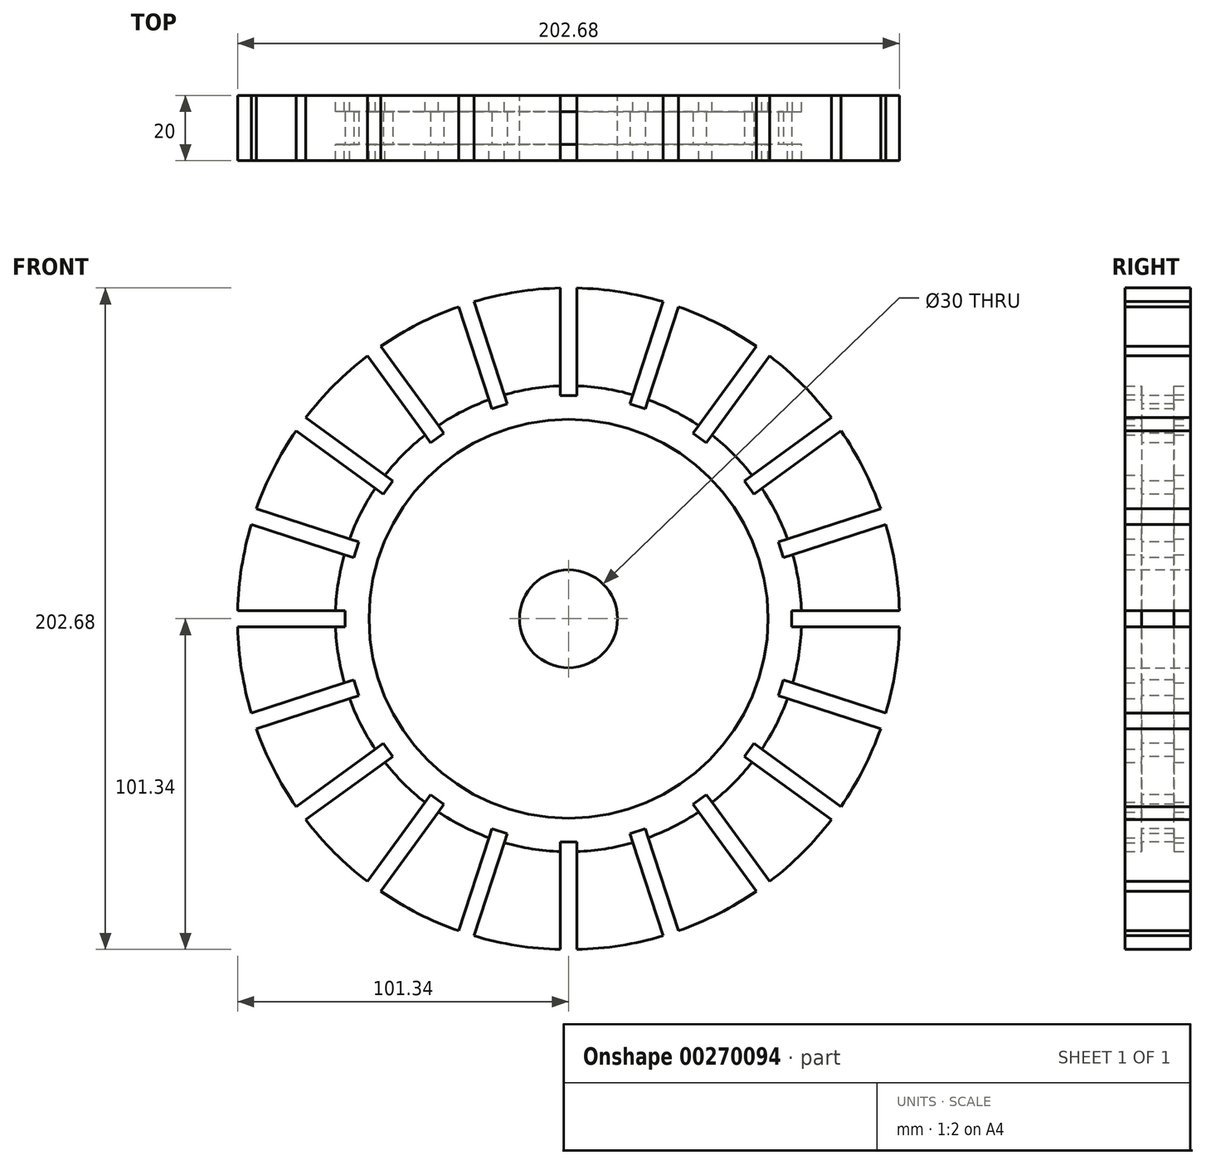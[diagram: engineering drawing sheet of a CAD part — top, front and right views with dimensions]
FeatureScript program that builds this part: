
annotation { "Feature Type Name" : "Feature", "Feature Type Description" : "" }
export const myFeature = defineFeature(function(context is Context, id is Id, definition is map)
    precondition{}
    {
        {
            var Q0;
            Q0=qCreatedBy(makeId("Right.planeOp"),FACE);
            var sketch = newSketch(context, id + "F0", { "sketchPlane" : qUnion([Q0])});
            skLineSegment(sketch, "E0", {"start": v(10, 15) * mm, "end": v(10, 61.1) * mm});
            skLineSegment(sketch, "E1", {"start": v(10, 61.1) * mm, "end": v(5, 61.1) * mm});
            skLineSegment(sketch, "E2", {"start": v(5, 61.1) * mm, "end": v(5, 71.4) * mm});
            skLineSegment(sketch, "E3", {"start": v(5, 71.4) * mm, "end": v(10, 71.4) * mm});
            skLineSegment(sketch, "E4", {"start": v(10, 71.4) * mm, "end": v(10, 101.37) * mm});
            skLineSegment(sketch, "E5", {"start": v(10, 101.37) * mm, "end": v(-10, 101.37) * mm});
            skLineSegment(sketch, "E6", {"start": v(-10, 15) * mm, "end": v(10, 15) * mm});
            skLineSegment(sketch, "E7", {"start": v(-10, 101.37) * mm, "end": v(-10, 71.4) * mm});
            skLineSegment(sketch, "E8", {"start": v(-10, 71.4) * mm, "end": v(-5, 71.4) * mm});
            skLineSegment(sketch, "E9", {"start": v(-5, 71.4) * mm, "end": v(-5, 61.1) * mm});
            skLineSegment(sketch, "E10", {"start": v(-5, 61.1) * mm, "end": v(-10, 61.1) * mm});
            skLineSegment(sketch, "E11", {"start": v(-10, 61.1) * mm, "end": v(-10, 15) * mm});
            skPoint(sketch, "E12", {"position": v(0, 15) * mm});
            skLineSegment(sketch, "E13", {"start": v(0, 0) * mm, "end": v(-55.9, 0) * mm, "construction": true});
            skSolve(sketch);
        }
        {
            var Q0;
            Q0=makeQuery(id+"F0.imprint","IMPRINT",FACE,{"disambiguationData":[TD([[makeQuery(id+"F0.imprint","IMPRINT",EDGE,{"derivedFrom":sQuery(id+"F0.wireOp",EDGE,"E0")}),1.0]])]});
            var Q1;
            Q1=sQuery(id+"F0.wireOp",EDGE,"E13");
            revolve(context, id + "F1", {"entities" : qUnion([Q0]), "axis" : qUnion([Q1]), "revolveType" : RevolveType.FULL});
        }
        {
            var Q0;
            Q0=makeQuery(id+"F1.opRevolve","SWEPT_FACE",FACE,{"disambiguationData":[OSD([sQuery(id+"F0.wireOp",EDGE,"E7")])]});
            var sketch = newSketch(context, id + "F2", { "sketchPlane" : qUnion([Q0])});
            skLineSegment(sketch, "E14", {"start": v(0, 0) * mm, "end": v(0, 127.9) * mm, "construction": true});
            skLineSegment(sketch, "E15.bottom", {"start": v(-2.5, 101.37) * mm, "end": v(2.5, 101.37) * mm});
            skLineSegment(sketch, "E15.top", {"start": v(-2.5, 68.4) * mm, "end": v(2.5, 68.4) * mm});
            skLineSegment(sketch, "E15.left", {"start": v(-2.5, 101.37) * mm, "end": v(-2.5, 68.4) * mm});
            skLineSegment(sketch, "E15.right", {"start": v(2.5, 101.37) * mm, "end": v(2.5, 68.4) * mm});
            skPoint(sketch, "E16", {"position": v(0, 101.37) * mm});
            skLineSegment(sketch, "E17", {"start": v(-18.81, 71.4) * mm, "end": v(18.81, 71.4) * mm, "construction": true});
            skPoint(sketch, "E18", {"position": v(0, 71.4) * mm});
            skLineSegment(sketch, "E19.1.0", {"start": v(-28.95, 97.18) * mm, "end": v(-18.76, 65.82) * mm});
            skLineSegment(sketch, "E19.1.1", {"start": v(-33.7, 95.64) * mm, "end": v(-23.51, 64.27) * mm});
            skLineSegment(sketch, "E19.1.2", {"start": v(-33.7, 95.64) * mm, "end": v(-28.95, 97.18) * mm});
            skLineSegment(sketch, "E19.1.3", {"start": v(-23.51, 64.27) * mm, "end": v(-18.76, 65.82) * mm});
            skLineSegment(sketch, "E19.2.0", {"start": v(-57.56, 83.48) * mm, "end": v(-38.18, 56.8) * mm});
            skLineSegment(sketch, "E19.2.1", {"start": v(-61.6, 80.54) * mm, "end": v(-42.22, 53.86) * mm});
            skLineSegment(sketch, "E19.2.2", {"start": v(-61.6, 80.54) * mm, "end": v(-57.56, 83.48) * mm});
            skLineSegment(sketch, "E19.2.3", {"start": v(-42.22, 53.86) * mm, "end": v(-38.18, 56.8) * mm});
            skLineSegment(sketch, "E19.3.0", {"start": v(-80.54, 61.6) * mm, "end": v(-53.86, 42.22) * mm});
            skLineSegment(sketch, "E19.3.1", {"start": v(-83.48, 57.56) * mm, "end": v(-56.8, 38.18) * mm});
            skLineSegment(sketch, "E19.3.2", {"start": v(-83.48, 57.56) * mm, "end": v(-80.54, 61.6) * mm});
            skLineSegment(sketch, "E19.3.3", {"start": v(-56.8, 38.18) * mm, "end": v(-53.86, 42.22) * mm});
            skLineSegment(sketch, "E19.4.0", {"start": v(-95.64, 33.7) * mm, "end": v(-64.27, 23.51) * mm});
            skLineSegment(sketch, "E19.4.1", {"start": v(-97.18, 28.95) * mm, "end": v(-65.82, 18.76) * mm});
            skLineSegment(sketch, "E19.4.2", {"start": v(-97.18, 28.95) * mm, "end": v(-95.64, 33.7) * mm});
            skLineSegment(sketch, "E19.4.3", {"start": v(-65.82, 18.76) * mm, "end": v(-64.27, 23.51) * mm});
            skLineSegment(sketch, "E19.5.0", {"start": v(-101.37, 2.5) * mm, "end": v(-68.4, 2.5) * mm});
            skLineSegment(sketch, "E19.5.1", {"start": v(-101.37, -2.5) * mm, "end": v(-68.4, -2.5) * mm});
            skLineSegment(sketch, "E19.5.2", {"start": v(-101.37, -2.5) * mm, "end": v(-101.37, 2.5) * mm});
            skLineSegment(sketch, "E19.5.3", {"start": v(-68.4, -2.5) * mm, "end": v(-68.4, 2.5) * mm});
            skLineSegment(sketch, "E19.6.0", {"start": v(-97.18, -28.95) * mm, "end": v(-65.82, -18.76) * mm});
            skLineSegment(sketch, "E19.6.1", {"start": v(-95.64, -33.7) * mm, "end": v(-64.27, -23.51) * mm});
            skLineSegment(sketch, "E19.6.2", {"start": v(-95.64, -33.7) * mm, "end": v(-97.18, -28.95) * mm});
            skLineSegment(sketch, "E19.6.3", {"start": v(-64.27, -23.51) * mm, "end": v(-65.82, -18.76) * mm});
            skLineSegment(sketch, "E19.7.0", {"start": v(-83.48, -57.56) * mm, "end": v(-56.8, -38.18) * mm});
            skLineSegment(sketch, "E19.7.1", {"start": v(-80.54, -61.6) * mm, "end": v(-53.86, -42.22) * mm});
            skLineSegment(sketch, "E19.7.2", {"start": v(-80.54, -61.6) * mm, "end": v(-83.48, -57.56) * mm});
            skLineSegment(sketch, "E19.7.3", {"start": v(-53.86, -42.22) * mm, "end": v(-56.8, -38.18) * mm});
            skLineSegment(sketch, "E19.8.0", {"start": v(-61.6, -80.54) * mm, "end": v(-42.22, -53.86) * mm});
            skLineSegment(sketch, "E19.8.1", {"start": v(-57.56, -83.48) * mm, "end": v(-38.18, -56.8) * mm});
            skLineSegment(sketch, "E19.8.2", {"start": v(-57.56, -83.48) * mm, "end": v(-61.6, -80.54) * mm});
            skLineSegment(sketch, "E19.8.3", {"start": v(-38.18, -56.8) * mm, "end": v(-42.22, -53.86) * mm});
            skLineSegment(sketch, "E19.9.0", {"start": v(-33.7, -95.64) * mm, "end": v(-23.51, -64.27) * mm});
            skLineSegment(sketch, "E19.9.1", {"start": v(-28.95, -97.18) * mm, "end": v(-18.76, -65.82) * mm});
            skLineSegment(sketch, "E19.9.2", {"start": v(-28.95, -97.18) * mm, "end": v(-33.7, -95.64) * mm});
            skLineSegment(sketch, "E19.9.3", {"start": v(-18.76, -65.82) * mm, "end": v(-23.51, -64.27) * mm});
            skLineSegment(sketch, "E19.10.0", {"start": v(-2.5, -101.37) * mm, "end": v(-2.5, -68.4) * mm});
            skLineSegment(sketch, "E19.10.1", {"start": v(2.5, -101.37) * mm, "end": v(2.5, -68.4) * mm});
            skLineSegment(sketch, "E19.10.2", {"start": v(2.5, -101.37) * mm, "end": v(-2.5, -101.37) * mm});
            skLineSegment(sketch, "E19.10.3", {"start": v(2.5, -68.4) * mm, "end": v(-2.5, -68.4) * mm});
            skLineSegment(sketch, "E19.11.0", {"start": v(28.95, -97.18) * mm, "end": v(18.76, -65.82) * mm});
            skLineSegment(sketch, "E19.11.1", {"start": v(33.7, -95.64) * mm, "end": v(23.51, -64.27) * mm});
            skLineSegment(sketch, "E19.11.2", {"start": v(33.7, -95.64) * mm, "end": v(28.95, -97.18) * mm});
            skLineSegment(sketch, "E19.11.3", {"start": v(23.51, -64.27) * mm, "end": v(18.76, -65.82) * mm});
            skLineSegment(sketch, "E19.12.0", {"start": v(57.56, -83.48) * mm, "end": v(38.18, -56.8) * mm});
            skLineSegment(sketch, "E19.12.1", {"start": v(61.6, -80.54) * mm, "end": v(42.22, -53.86) * mm});
            skLineSegment(sketch, "E19.12.2", {"start": v(61.6, -80.54) * mm, "end": v(57.56, -83.48) * mm});
            skLineSegment(sketch, "E19.12.3", {"start": v(42.22, -53.86) * mm, "end": v(38.18, -56.8) * mm});
            skLineSegment(sketch, "E19.13.0", {"start": v(80.54, -61.6) * mm, "end": v(53.86, -42.22) * mm});
            skLineSegment(sketch, "E19.13.1", {"start": v(83.48, -57.56) * mm, "end": v(56.8, -38.18) * mm});
            skLineSegment(sketch, "E19.13.2", {"start": v(83.48, -57.56) * mm, "end": v(80.54, -61.6) * mm});
            skLineSegment(sketch, "E19.13.3", {"start": v(56.8, -38.18) * mm, "end": v(53.86, -42.22) * mm});
            skLineSegment(sketch, "E19.14.0", {"start": v(95.64, -33.7) * mm, "end": v(64.27, -23.51) * mm});
            skLineSegment(sketch, "E19.14.1", {"start": v(97.18, -28.95) * mm, "end": v(65.82, -18.76) * mm});
            skLineSegment(sketch, "E19.14.2", {"start": v(97.18, -28.95) * mm, "end": v(95.64, -33.7) * mm});
            skLineSegment(sketch, "E19.14.3", {"start": v(65.82, -18.76) * mm, "end": v(64.27, -23.51) * mm});
            skLineSegment(sketch, "E19.15.0", {"start": v(101.37, -2.5) * mm, "end": v(68.4, -2.5) * mm});
            skLineSegment(sketch, "E19.15.1", {"start": v(101.37, 2.5) * mm, "end": v(68.4, 2.5) * mm});
            skLineSegment(sketch, "E19.15.2", {"start": v(101.37, 2.5) * mm, "end": v(101.37, -2.5) * mm});
            skLineSegment(sketch, "E19.15.3", {"start": v(68.4, 2.5) * mm, "end": v(68.4, -2.5) * mm});
            skLineSegment(sketch, "E19.16.0", {"start": v(97.18, 28.95) * mm, "end": v(65.82, 18.76) * mm});
            skLineSegment(sketch, "E19.16.1", {"start": v(95.64, 33.7) * mm, "end": v(64.27, 23.51) * mm});
            skLineSegment(sketch, "E19.16.2", {"start": v(95.64, 33.7) * mm, "end": v(97.18, 28.95) * mm});
            skLineSegment(sketch, "E19.16.3", {"start": v(64.27, 23.51) * mm, "end": v(65.82, 18.76) * mm});
            skLineSegment(sketch, "E19.17.0", {"start": v(83.48, 57.56) * mm, "end": v(56.8, 38.18) * mm});
            skLineSegment(sketch, "E19.17.1", {"start": v(80.54, 61.6) * mm, "end": v(53.86, 42.22) * mm});
            skLineSegment(sketch, "E19.17.2", {"start": v(80.54, 61.6) * mm, "end": v(83.48, 57.56) * mm});
            skLineSegment(sketch, "E19.17.3", {"start": v(53.86, 42.22) * mm, "end": v(56.8, 38.18) * mm});
            skLineSegment(sketch, "E19.18.0", {"start": v(61.6, 80.54) * mm, "end": v(42.22, 53.86) * mm});
            skLineSegment(sketch, "E19.18.1", {"start": v(57.56, 83.48) * mm, "end": v(38.18, 56.8) * mm});
            skLineSegment(sketch, "E19.18.2", {"start": v(57.56, 83.48) * mm, "end": v(61.6, 80.54) * mm});
            skLineSegment(sketch, "E19.18.3", {"start": v(38.18, 56.8) * mm, "end": v(42.22, 53.86) * mm});
            skLineSegment(sketch, "E19.19.0", {"start": v(33.7, 95.64) * mm, "end": v(23.51, 64.27) * mm});
            skLineSegment(sketch, "E19.19.1", {"start": v(28.95, 97.18) * mm, "end": v(18.76, 65.82) * mm});
            skLineSegment(sketch, "E19.19.2", {"start": v(28.95, 97.18) * mm, "end": v(33.7, 95.64) * mm});
            skLineSegment(sketch, "E19.19.3", {"start": v(18.76, 65.82) * mm, "end": v(23.51, 64.27) * mm});
            skPoint(sketch, "E19.center", {"position": v(0, 0) * mm});
            skSolve(sketch);
        }
        {
            var Q0;
            {var subQ0=sQuery(id+"F0.wireOp",EDGE,"E7");var subQ1=makeQuery(id+"F1.opRevolve","SWEPT_EDGE",EDGE,{"disambiguationData":[OSD([sQuery(id+"F0.wireOp",EDGE,"E5"),subQ0])]});var subQ5=sQuery(id+"F2.wireOp",EDGE,"E15.left");var subQ6=makeQuery(id+"F2.imprint","INTERSECT",VERTEX,{"derivedFrom":[subQ1,subQ5]});Q0=makeQuery(id+"F2.imprint","IMPRINT",FACE,{"disambiguationData":[TD([[makeQuery(id+"F2.imprint","IMPRINT",EDGE,{"disambiguationData":[TD([[subQ6,-1.0]])],"derivedFrom":subQ5}),1.0]])]});}
            var Q1;
            {var subQ0=sQuery(id+"F2.wireOp",EDGE,"E15.top");Q1=makeQuery(id+"F2.imprint","IMPRINT",FACE,{"disambiguationData":[TD([[makeQuery(id+"F2.imprint","IMPRINT",EDGE,{"derivedFrom":subQ0}),1.0]])]});}
            var Q2;
            {var subQ1=sQuery(id+"F0.wireOp",EDGE,"E7");var subQ2=makeQuery(id+"F1.opRevolve","SWEPT_EDGE",EDGE,{"disambiguationData":[OSD([sQuery(id+"F0.wireOp",EDGE,"E5"),subQ1])]});var subQ5=sQuery(id+"F2.wireOp",EDGE,"E19.19.0");var subQ6=makeQuery(id+"F2.imprint","INTERSECT",VERTEX,{"derivedFrom":[subQ2,subQ5]});Q2=makeQuery(id+"F2.imprint","IMPRINT",FACE,{"disambiguationData":[TD([[makeQuery(id+"F2.imprint","IMPRINT",EDGE,{"disambiguationData":[TD([[subQ6,-1.0]])],"derivedFrom":subQ5}),-1.0]])]});}
            var Q3;
            {var subQ0=sQuery(id+"F2.wireOp",EDGE,"E19.19.3");Q3=makeQuery(id+"F2.imprint","IMPRINT",FACE,{"disambiguationData":[TD([[makeQuery(id+"F2.imprint","IMPRINT",EDGE,{"derivedFrom":subQ0}),1.0]])]});}
            var Q4;
            {var subQ1=sQuery(id+"F0.wireOp",EDGE,"E7");var subQ2=makeQuery(id+"F1.opRevolve","SWEPT_EDGE",EDGE,{"disambiguationData":[OSD([sQuery(id+"F0.wireOp",EDGE,"E5"),subQ1])]});var subQ5=sQuery(id+"F2.wireOp",EDGE,"E19.18.0");var subQ6=makeQuery(id+"F2.imprint","INTERSECT",VERTEX,{"derivedFrom":[subQ2,subQ5]});Q4=makeQuery(id+"F2.imprint","IMPRINT",FACE,{"disambiguationData":[TD([[makeQuery(id+"F2.imprint","IMPRINT",EDGE,{"disambiguationData":[TD([[subQ6,-1.0]])],"derivedFrom":subQ5}),-1.0]])]});}
            var Q5;
            {var subQ0=sQuery(id+"F2.wireOp",EDGE,"E19.18.3");Q5=makeQuery(id+"F2.imprint","IMPRINT",FACE,{"disambiguationData":[TD([[makeQuery(id+"F2.imprint","IMPRINT",EDGE,{"derivedFrom":subQ0}),1.0]])]});}
            var Q6;
            {var subQ1=sQuery(id+"F0.wireOp",EDGE,"E7");var subQ2=makeQuery(id+"F1.opRevolve","SWEPT_EDGE",EDGE,{"disambiguationData":[OSD([sQuery(id+"F0.wireOp",EDGE,"E5"),subQ1])]});var subQ5=sQuery(id+"F2.wireOp",EDGE,"E19.17.0");var subQ6=makeQuery(id+"F2.imprint","INTERSECT",VERTEX,{"derivedFrom":[subQ2,subQ5]});Q6=makeQuery(id+"F2.imprint","IMPRINT",FACE,{"disambiguationData":[TD([[makeQuery(id+"F2.imprint","IMPRINT",EDGE,{"disambiguationData":[TD([[subQ6,-1.0]])],"derivedFrom":subQ5}),-1.0]])]});}
            var Q7;
            {var subQ0=sQuery(id+"F2.wireOp",EDGE,"E19.17.3");Q7=makeQuery(id+"F2.imprint","IMPRINT",FACE,{"disambiguationData":[TD([[makeQuery(id+"F2.imprint","IMPRINT",EDGE,{"derivedFrom":subQ0}),1.0]])]});}
            var Q8;
            {var subQ1=sQuery(id+"F0.wireOp",EDGE,"E7");var subQ2=makeQuery(id+"F1.opRevolve","SWEPT_EDGE",EDGE,{"disambiguationData":[OSD([sQuery(id+"F0.wireOp",EDGE,"E5"),subQ1])]});var subQ7=sQuery(id+"F2.wireOp",EDGE,"E19.16.0");var subQ8=makeQuery(id+"F2.imprint","INTERSECT",VERTEX,{"derivedFrom":[subQ2,subQ7]});Q8=makeQuery(id+"F2.imprint","IMPRINT",FACE,{"disambiguationData":[TD([[makeQuery(id+"F2.imprint","IMPRINT",EDGE,{"disambiguationData":[TD([[subQ8,-1.0]])],"derivedFrom":subQ7}),-1.0]])]});}
            var Q9;
            {var subQ0=sQuery(id+"F2.wireOp",EDGE,"E19.16.3");Q9=makeQuery(id+"F2.imprint","IMPRINT",FACE,{"disambiguationData":[TD([[makeQuery(id+"F2.imprint","IMPRINT",EDGE,{"derivedFrom":subQ0}),1.0]])]});}
            var Q10;
            {var subQ1=sQuery(id+"F0.wireOp",EDGE,"E7");var subQ2=makeQuery(id+"F1.opRevolve","SWEPT_EDGE",EDGE,{"disambiguationData":[OSD([sQuery(id+"F0.wireOp",EDGE,"E5"),subQ1])]});var subQ5=sQuery(id+"F2.wireOp",EDGE,"E19.15.0");var subQ6=makeQuery(id+"F2.imprint","INTERSECT",VERTEX,{"derivedFrom":[subQ2,subQ5]});Q10=makeQuery(id+"F2.imprint","IMPRINT",FACE,{"disambiguationData":[TD([[makeQuery(id+"F2.imprint","IMPRINT",EDGE,{"disambiguationData":[TD([[subQ6,-1.0]])],"derivedFrom":subQ5}),-1.0]])]});}
            var Q11;
            {var subQ0=sQuery(id+"F2.wireOp",EDGE,"E19.15.3");Q11=makeQuery(id+"F2.imprint","IMPRINT",FACE,{"disambiguationData":[TD([[makeQuery(id+"F2.imprint","IMPRINT",EDGE,{"derivedFrom":subQ0}),1.0]])]});}
            var Q12;
            {var subQ1=sQuery(id+"F0.wireOp",EDGE,"E7");var subQ2=makeQuery(id+"F1.opRevolve","SWEPT_EDGE",EDGE,{"disambiguationData":[OSD([sQuery(id+"F0.wireOp",EDGE,"E5"),subQ1])]});var subQ5=sQuery(id+"F2.wireOp",EDGE,"E19.14.0");var subQ6=makeQuery(id+"F2.imprint","INTERSECT",VERTEX,{"derivedFrom":[subQ2,subQ5]});Q12=makeQuery(id+"F2.imprint","IMPRINT",FACE,{"disambiguationData":[TD([[makeQuery(id+"F2.imprint","IMPRINT",EDGE,{"disambiguationData":[TD([[subQ6,-1.0]])],"derivedFrom":subQ5}),-1.0]])]});}
            var Q13;
            {var subQ0=sQuery(id+"F2.wireOp",EDGE,"E19.14.3");Q13=makeQuery(id+"F2.imprint","IMPRINT",FACE,{"disambiguationData":[TD([[makeQuery(id+"F2.imprint","IMPRINT",EDGE,{"derivedFrom":subQ0}),1.0]])]});}
            var Q14;
            {var subQ1=sQuery(id+"F0.wireOp",EDGE,"E7");var subQ2=makeQuery(id+"F1.opRevolve","SWEPT_EDGE",EDGE,{"disambiguationData":[OSD([sQuery(id+"F0.wireOp",EDGE,"E5"),subQ1])]});var subQ5=sQuery(id+"F2.wireOp",EDGE,"E19.13.0");var subQ6=makeQuery(id+"F2.imprint","INTERSECT",VERTEX,{"derivedFrom":[subQ2,subQ5]});Q14=makeQuery(id+"F2.imprint","IMPRINT",FACE,{"disambiguationData":[TD([[makeQuery(id+"F2.imprint","IMPRINT",EDGE,{"disambiguationData":[TD([[subQ6,-1.0]])],"derivedFrom":subQ5}),-1.0]])]});}
            var Q15;
            {var subQ0=sQuery(id+"F2.wireOp",EDGE,"E19.13.3");Q15=makeQuery(id+"F2.imprint","IMPRINT",FACE,{"disambiguationData":[TD([[makeQuery(id+"F2.imprint","IMPRINT",EDGE,{"derivedFrom":subQ0}),1.0]])]});}
            var Q16;
            {var subQ1=sQuery(id+"F0.wireOp",EDGE,"E7");var subQ2=makeQuery(id+"F1.opRevolve","SWEPT_EDGE",EDGE,{"disambiguationData":[OSD([sQuery(id+"F0.wireOp",EDGE,"E5"),subQ1])]});var subQ7=sQuery(id+"F2.wireOp",EDGE,"E19.12.0");var subQ8=makeQuery(id+"F2.imprint","INTERSECT",VERTEX,{"derivedFrom":[subQ2,subQ7]});Q16=makeQuery(id+"F2.imprint","IMPRINT",FACE,{"disambiguationData":[TD([[makeQuery(id+"F2.imprint","IMPRINT",EDGE,{"disambiguationData":[TD([[subQ8,-1.0]])],"derivedFrom":subQ7}),-1.0]])]});}
            var Q17;
            {var subQ0=sQuery(id+"F2.wireOp",EDGE,"E19.12.3");Q17=makeQuery(id+"F2.imprint","IMPRINT",FACE,{"disambiguationData":[TD([[makeQuery(id+"F2.imprint","IMPRINT",EDGE,{"derivedFrom":subQ0}),1.0]])]});}
            var Q18;
            {var subQ1=sQuery(id+"F0.wireOp",EDGE,"E7");var subQ2=makeQuery(id+"F1.opRevolve","SWEPT_EDGE",EDGE,{"disambiguationData":[OSD([sQuery(id+"F0.wireOp",EDGE,"E5"),subQ1])]});var subQ7=sQuery(id+"F2.wireOp",EDGE,"E19.11.0");var subQ8=makeQuery(id+"F2.imprint","INTERSECT",VERTEX,{"derivedFrom":[subQ2,subQ7]});Q18=makeQuery(id+"F2.imprint","IMPRINT",FACE,{"disambiguationData":[TD([[makeQuery(id+"F2.imprint","IMPRINT",EDGE,{"disambiguationData":[TD([[subQ8,-1.0]])],"derivedFrom":subQ7}),-1.0]])]});}
            var Q19;
            {var subQ0=sQuery(id+"F2.wireOp",EDGE,"E19.11.3");Q19=makeQuery(id+"F2.imprint","IMPRINT",FACE,{"disambiguationData":[TD([[makeQuery(id+"F2.imprint","IMPRINT",EDGE,{"derivedFrom":subQ0}),1.0]])]});}
            var Q20;
            {var subQ1=sQuery(id+"F0.wireOp",EDGE,"E7");var subQ2=makeQuery(id+"F1.opRevolve","SWEPT_EDGE",EDGE,{"disambiguationData":[OSD([sQuery(id+"F0.wireOp",EDGE,"E5"),subQ1])]});var subQ7=sQuery(id+"F2.wireOp",EDGE,"E19.10.0");var subQ8=makeQuery(id+"F2.imprint","INTERSECT",VERTEX,{"derivedFrom":[subQ2,subQ7]});Q20=makeQuery(id+"F2.imprint","IMPRINT",FACE,{"disambiguationData":[TD([[makeQuery(id+"F2.imprint","IMPRINT",EDGE,{"disambiguationData":[TD([[subQ8,-1.0]])],"derivedFrom":subQ7}),-1.0]])]});}
            var Q21;
            {var subQ0=sQuery(id+"F2.wireOp",EDGE,"E19.10.3");Q21=makeQuery(id+"F2.imprint","IMPRINT",FACE,{"disambiguationData":[TD([[makeQuery(id+"F2.imprint","IMPRINT",EDGE,{"derivedFrom":subQ0}),1.0]])]});}
            var Q22;
            {var subQ1=sQuery(id+"F0.wireOp",EDGE,"E7");var subQ2=makeQuery(id+"F1.opRevolve","SWEPT_EDGE",EDGE,{"disambiguationData":[OSD([sQuery(id+"F0.wireOp",EDGE,"E5"),subQ1])]});var subQ7=sQuery(id+"F2.wireOp",EDGE,"E19.9.0");var subQ8=makeQuery(id+"F2.imprint","INTERSECT",VERTEX,{"derivedFrom":[subQ2,subQ7]});Q22=makeQuery(id+"F2.imprint","IMPRINT",FACE,{"disambiguationData":[TD([[makeQuery(id+"F2.imprint","IMPRINT",EDGE,{"disambiguationData":[TD([[subQ8,-1.0]])],"derivedFrom":subQ7}),-1.0]])]});}
            var Q23;
            {var subQ0=sQuery(id+"F2.wireOp",EDGE,"E19.9.3");Q23=makeQuery(id+"F2.imprint","IMPRINT",FACE,{"disambiguationData":[TD([[makeQuery(id+"F2.imprint","IMPRINT",EDGE,{"derivedFrom":subQ0}),1.0]])]});}
            var Q24;
            {var subQ1=sQuery(id+"F0.wireOp",EDGE,"E7");var subQ2=makeQuery(id+"F1.opRevolve","SWEPT_EDGE",EDGE,{"disambiguationData":[OSD([sQuery(id+"F0.wireOp",EDGE,"E5"),subQ1])]});var subQ5=sQuery(id+"F2.wireOp",EDGE,"E19.8.0");var subQ6=makeQuery(id+"F2.imprint","INTERSECT",VERTEX,{"derivedFrom":[subQ2,subQ5]});Q24=makeQuery(id+"F2.imprint","IMPRINT",FACE,{"disambiguationData":[TD([[makeQuery(id+"F2.imprint","IMPRINT",EDGE,{"disambiguationData":[TD([[subQ6,-1.0]])],"derivedFrom":subQ5}),-1.0]])]});}
            var Q25;
            {var subQ0=sQuery(id+"F2.wireOp",EDGE,"E19.8.3");Q25=makeQuery(id+"F2.imprint","IMPRINT",FACE,{"disambiguationData":[TD([[makeQuery(id+"F2.imprint","IMPRINT",EDGE,{"derivedFrom":subQ0}),1.0]])]});}
            var Q26;
            {var subQ0=sQuery(id+"F2.wireOp",EDGE,"E19.7.0");var subQ1=sQuery(id+"F0.wireOp",EDGE,"E7");var subQ2=makeQuery(id+"F1.opRevolve","SWEPT_EDGE",EDGE,{"disambiguationData":[OSD([sQuery(id+"F0.wireOp",EDGE,"E5"),subQ1])]});var subQ3=makeQuery(id+"F2.imprint","INTERSECT",VERTEX,{"derivedFrom":[subQ2,subQ0]});Q26=makeQuery(id+"F2.imprint","IMPRINT",FACE,{"disambiguationData":[TD([[makeQuery(id+"F2.imprint","IMPRINT",EDGE,{"disambiguationData":[TD([[subQ3,-1.0]])],"derivedFrom":subQ0}),-1.0]])]});}
            var Q27;
            {var subQ0=sQuery(id+"F2.wireOp",EDGE,"E19.7.3");Q27=makeQuery(id+"F2.imprint","IMPRINT",FACE,{"disambiguationData":[TD([[makeQuery(id+"F2.imprint","IMPRINT",EDGE,{"derivedFrom":subQ0}),1.0]])]});}
            var Q28;
            {var subQ1=sQuery(id+"F0.wireOp",EDGE,"E7");var subQ2=makeQuery(id+"F1.opRevolve","SWEPT_EDGE",EDGE,{"disambiguationData":[OSD([sQuery(id+"F0.wireOp",EDGE,"E5"),subQ1])]});var subQ5=sQuery(id+"F2.wireOp",EDGE,"E19.6.0");var subQ6=makeQuery(id+"F2.imprint","INTERSECT",VERTEX,{"derivedFrom":[subQ2,subQ5]});Q28=makeQuery(id+"F2.imprint","IMPRINT",FACE,{"disambiguationData":[TD([[makeQuery(id+"F2.imprint","IMPRINT",EDGE,{"disambiguationData":[TD([[subQ6,-1.0]])],"derivedFrom":subQ5}),-1.0]])]});}
            var Q29;
            {var subQ0=sQuery(id+"F2.wireOp",EDGE,"E19.6.3");Q29=makeQuery(id+"F2.imprint","IMPRINT",FACE,{"disambiguationData":[TD([[makeQuery(id+"F2.imprint","IMPRINT",EDGE,{"derivedFrom":subQ0}),1.0]])]});}
            var Q30;
            {var subQ1=sQuery(id+"F0.wireOp",EDGE,"E7");var subQ2=makeQuery(id+"F1.opRevolve","SWEPT_EDGE",EDGE,{"disambiguationData":[OSD([sQuery(id+"F0.wireOp",EDGE,"E5"),subQ1])]});var subQ5=sQuery(id+"F2.wireOp",EDGE,"E19.5.0");var subQ6=makeQuery(id+"F2.imprint","INTERSECT",VERTEX,{"derivedFrom":[subQ2,subQ5]});Q30=makeQuery(id+"F2.imprint","IMPRINT",FACE,{"disambiguationData":[TD([[makeQuery(id+"F2.imprint","IMPRINT",EDGE,{"disambiguationData":[TD([[subQ6,-1.0]])],"derivedFrom":subQ5}),-1.0]])]});}
            var Q31;
            {var subQ0=sQuery(id+"F2.wireOp",EDGE,"E19.5.3");Q31=makeQuery(id+"F2.imprint","IMPRINT",FACE,{"disambiguationData":[TD([[makeQuery(id+"F2.imprint","IMPRINT",EDGE,{"derivedFrom":subQ0}),1.0]])]});}
            var Q32;
            {var subQ0=sQuery(id+"F2.wireOp",EDGE,"E19.4.0");var subQ1=sQuery(id+"F0.wireOp",EDGE,"E7");var subQ2=makeQuery(id+"F1.opRevolve","SWEPT_EDGE",EDGE,{"disambiguationData":[OSD([sQuery(id+"F0.wireOp",EDGE,"E5"),subQ1])]});var subQ3=makeQuery(id+"F2.imprint","INTERSECT",VERTEX,{"derivedFrom":[subQ2,subQ0]});Q32=makeQuery(id+"F2.imprint","IMPRINT",FACE,{"disambiguationData":[TD([[makeQuery(id+"F2.imprint","IMPRINT",EDGE,{"disambiguationData":[TD([[subQ3,-1.0]])],"derivedFrom":subQ0}),-1.0]])]});}
            var Q33;
            {var subQ0=sQuery(id+"F2.wireOp",EDGE,"E19.4.3");Q33=makeQuery(id+"F2.imprint","IMPRINT",FACE,{"disambiguationData":[TD([[makeQuery(id+"F2.imprint","IMPRINT",EDGE,{"derivedFrom":subQ0}),1.0]])]});}
            var Q34;
            {var subQ1=sQuery(id+"F0.wireOp",EDGE,"E7");var subQ2=makeQuery(id+"F1.opRevolve","SWEPT_EDGE",EDGE,{"disambiguationData":[OSD([sQuery(id+"F0.wireOp",EDGE,"E5"),subQ1])]});var subQ5=sQuery(id+"F2.wireOp",EDGE,"E19.3.0");var subQ6=makeQuery(id+"F2.imprint","INTERSECT",VERTEX,{"derivedFrom":[subQ2,subQ5]});Q34=makeQuery(id+"F2.imprint","IMPRINT",FACE,{"disambiguationData":[TD([[makeQuery(id+"F2.imprint","IMPRINT",EDGE,{"disambiguationData":[TD([[subQ6,-1.0]])],"derivedFrom":subQ5}),-1.0]])]});}
            var Q35;
            {var subQ0=sQuery(id+"F2.wireOp",EDGE,"E19.3.3");Q35=makeQuery(id+"F2.imprint","IMPRINT",FACE,{"disambiguationData":[TD([[makeQuery(id+"F2.imprint","IMPRINT",EDGE,{"derivedFrom":subQ0}),1.0]])]});}
            var Q36;
            {var subQ1=sQuery(id+"F0.wireOp",EDGE,"E7");var subQ2=makeQuery(id+"F1.opRevolve","SWEPT_EDGE",EDGE,{"disambiguationData":[OSD([sQuery(id+"F0.wireOp",EDGE,"E5"),subQ1])]});var subQ7=sQuery(id+"F2.wireOp",EDGE,"E19.2.0");var subQ8=makeQuery(id+"F2.imprint","INTERSECT",VERTEX,{"derivedFrom":[subQ2,subQ7]});Q36=makeQuery(id+"F2.imprint","IMPRINT",FACE,{"disambiguationData":[TD([[makeQuery(id+"F2.imprint","IMPRINT",EDGE,{"disambiguationData":[TD([[subQ8,-1.0]])],"derivedFrom":subQ7}),-1.0]])]});}
            var Q37;
            {var subQ0=sQuery(id+"F2.wireOp",EDGE,"E19.2.3");Q37=makeQuery(id+"F2.imprint","IMPRINT",FACE,{"disambiguationData":[TD([[makeQuery(id+"F2.imprint","IMPRINT",EDGE,{"derivedFrom":subQ0}),1.0]])]});}
            var Q38;
            {var subQ1=sQuery(id+"F0.wireOp",EDGE,"E7");var subQ2=makeQuery(id+"F1.opRevolve","SWEPT_EDGE",EDGE,{"disambiguationData":[OSD([sQuery(id+"F0.wireOp",EDGE,"E5"),subQ1])]});var subQ5=sQuery(id+"F2.wireOp",EDGE,"E19.1.0");var subQ6=makeQuery(id+"F2.imprint","INTERSECT",VERTEX,{"derivedFrom":[subQ2,subQ5]});Q38=makeQuery(id+"F2.imprint","IMPRINT",FACE,{"disambiguationData":[TD([[makeQuery(id+"F2.imprint","IMPRINT",EDGE,{"disambiguationData":[TD([[subQ6,-1.0]])],"derivedFrom":subQ5}),-1.0]])]});}
            var Q39;
            {var subQ0=sQuery(id+"F2.wireOp",EDGE,"E19.1.3");Q39=makeQuery(id+"F2.imprint","IMPRINT",FACE,{"disambiguationData":[TD([[makeQuery(id+"F2.imprint","IMPRINT",EDGE,{"derivedFrom":subQ0}),1.0]])]});}
            var Q40;
            Q40=makeQuery(id+"F1.opRevolve","SWEPT_FACE",FACE,{"disambiguationData":[OSD([sQuery(id+"F0.wireOp",EDGE,"E4")])]});
            extrude(context, id + "F3", {"entities" : qUnion([Q0, Q1, Q2, Q3, Q4, Q5, Q6, Q7, Q8, Q9, Q10, Q11, Q12, Q13, Q14, Q15, Q16, Q17, Q18, Q19, Q20, Q21, Q22, Q23, Q24, Q25, Q26, Q27, Q28, Q29, Q30, Q31, Q32, Q33, Q34, Q35, Q36, Q37, Q38, Q39]), "operationType" : NewBodyOperationType.REMOVE, "endBound" : BoundingType.UP_TO_SURFACE, "oppositeDirection" : true, "endBoundEntityFace" : qUnion([Q40]), "depth" : 25 * mm});
        }
    });
